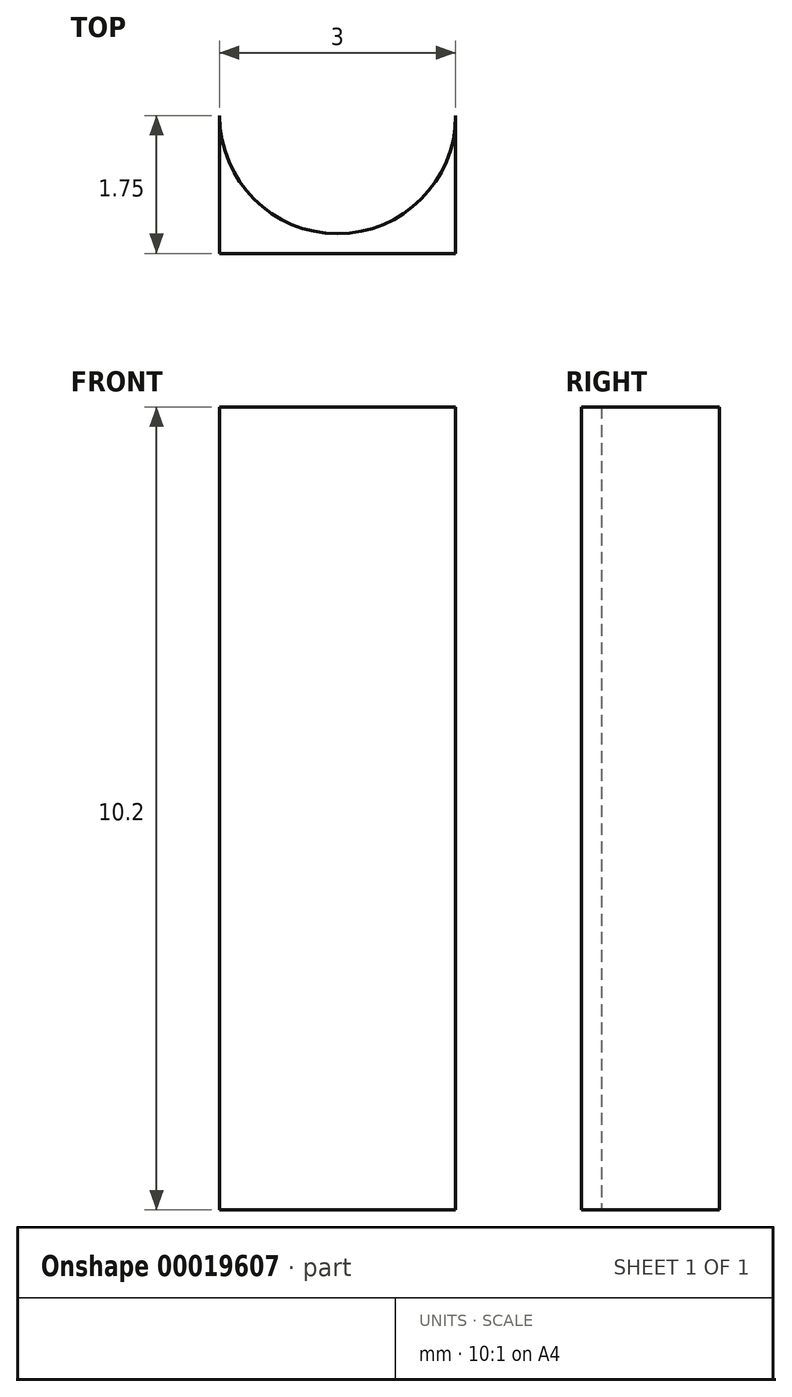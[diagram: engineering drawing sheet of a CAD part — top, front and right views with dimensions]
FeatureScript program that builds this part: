
annotation { "Feature Type Name" : "Feature", "Feature Type Description" : "" }
export const myFeature = defineFeature(function(context is Context, id is Id, definition is map)
    precondition{}
    {
        {
            var Q0;
            Q0=qCreatedBy(makeId("Top.planeOp"),FACE);
            var sketch = newSketch(context, id + "F0", { "sketchPlane" : qUnion([Q0])});
            skLineSegment(sketch, "E0.rect.top", {"start": v(-1.5, -1.75) * mm, "end": v(1.5, -1.75) * mm});
            skLineSegment(sketch, "E0.rect.left", {"start": v(-1.5, 0) * mm, "end": v(-1.5, -1.75) * mm});
            skLineSegment(sketch, "E0.rect.right", {"start": v(1.5, 0) * mm, "end": v(1.5, -1.75) * mm});
            skPoint(sketch, "E0.rect.middle", {"position": v(0, 0) * mm});
            skArc(sketch, "E1", {"start": v(-1.5, 0) * mm, "mid": v(0, -1.5) * mm, "end": v(1.5, 0) * mm});
            skPoint(sketch, "E0.rect.bottom.start.orphan", {"position": v(-1.5, 1.75) * mm});
            skPoint(sketch, "E2.orphan", {"position": v(1.5, 1.75) * mm});
            skSolve(sketch);
        }
        {
            var Q0;
            Q0=makeQuery(id+"F0.imprint","IMPRINT",FACE,{"disambiguationData":[TD([[makeQuery(id+"F0.imprint","IMPRINT",EDGE,{"derivedFrom":sQuery(id+"F0.wireOp",EDGE,"E0.rect.top")}),1.0]])]});
            extrude(context, id + "F1", {"entities" : qUnion([Q0]), "depth" : 10.2 * mm});
        }
    });
